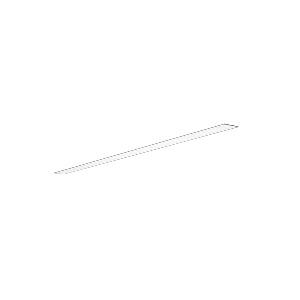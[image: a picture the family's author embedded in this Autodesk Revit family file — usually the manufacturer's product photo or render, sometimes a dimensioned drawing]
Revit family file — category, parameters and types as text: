
# Revit family: dotoo_line_-_dle_2000_830_d_00808228_687f
name_source: partatom
category: Lighting Fixtures
units: mm (PartAtom-declared; Revit-internal decimal feet)

## family parameters
Cut with Voids When Loaded = No
Host = Face
Light Source = No
Part Type = Normal
Room Calculation Point = No
Round Connector Dimension = Use Diameter
Shared = No

## types (1)
- DOTOO.line - DLE 2000/830/D (1 x LED, 1650 lm, 3000K)
    Apparent Load = 16 VA
    Approval mark = CE
    CIE Flux Codes = 67 91 98 100 100
    Color Rendering = 80-89
    Color Temperature = 3000K
    Control Gear = Electronic ballast
    Default Elevation = 1800 mm
    Description = DLE 2000/830/D|Recessed luminaire|light source:  |work equipment: Adjustable electronic ballast, digital DALI|connected load: 220-240 V, 50/60 Hz|Power consumption: approx. 16 W|standby: approx. 0,20|power factor: approx. 0,970|luminous flux: 1650 lm|luminous efficacy: 103 lm/W|light distribution: Direct|direct ratio: approx. 100 %|colour temperature: Warm white, ca. 3000 K|color rendering index (CRI): >= 80|chromaticity tolerance:  3 SDCM|System of protection: IP 40|class of protection: I|technology: Continuously dimmable|operation: External|luminaire body|material: Sectional aluminium|colour: White|lamp cover: Acrylic (PMMA), Clear|weight (net): approx. 4.7 kg|mains lead: Connector|Fastening: Fastening bow|glare control: Prism aperture|luminance(L65): <= 3000 cd/m|unified glare rating(4H 8H): <=  19|special features: DALI Load 1x, TouchDIM - dimming via standard switch, Flicker-free, Suitable as emergency lighting|
    Frequency = 50 Hz
    Height = 0 mm  [stored 0 ft]
    Lamp = 1 x LED
    Lamp Light Flux = 1650 lm
    Lamp count = 1
    Length = 1414 mm
    Luminous efficacy = 103 lm/W
    Manufacturer = Waldmann
    ModVariant = No
    Model = 00808228
    Mounting Place = Ceiling
    Mounting Type = Recessed
    Number of Poles = 1
    OnlyDefault = Yes
    Power Factor = 1
    Product Name = DOTOO.line - DLE 2000/830/D
    Product group = Recessed luminaire
    ProductGroupID = 4
    Protection Class = Protection class I
    Protection Degree = IP 40
    RLX_Detail_Level = 1
    RLX_Emergency_Light_Flux = 0 lm
    RLX_Emergency_Type = 0
    RLX_Emergency_Type_DB = No
    RlxData = <blob elided: 13509 chars, md5=7523a6bf>
    Socket = socket
    Standby Power = 0 W
    System Light Flux = 1650 lm
    System Power = 16 W
    Type Comments = Product without accessories
    Type Image = 114406000-00808224.jpg
    URL = http://relux.com
    VarID = ---
    Voltage = 230 V
    Voltage Range = 220-240 V
    Weight = 0.00 kg
    Width = 60 mm  [stored 0.19685 ft]

note: [stored X ft] marks values corroborated as IEEE doubles in the binary element streams (Revit-internal decimal feet)

## geometry (parser evidence)
native form markers: Sweep x9
no freeform markers — native parametric forms only
